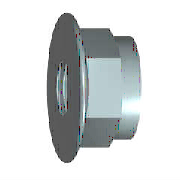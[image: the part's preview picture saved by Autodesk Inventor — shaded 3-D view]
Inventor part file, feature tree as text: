
AUTODESK INVENTOR PART (.ipt)
format: ipt  version: 2018 (Build 220112000, 112)  size: 214,016 bytes
history: native  units: mm (DEFAULTED — no unit token found)
features: other x3, sketch x3, extrude x2, hole x1, plane x1
ambient origin geometry x7: Origin, YZ Plane, XZ Plane, X Axis, Y Axis, Z Axis, Center Point
bodies: Solid1 (feature_tree)
feature tree (10):
  other  "Anello"
  extrude  "Corpo"  Depth=34.5mm
  extrude  "Corona"  Depth=2.4mm
  hole  "Filettatura"  [1 undecoded]
  other  "Smusso1"
  other  "Work Axis1"
  plane  "Work Plane1"
  sketch  "Schizzo1"
  sketch  "Schizzo5"
  sketch  "Schizzo3"
note: 1 required parameter value undecoded (feature->parameter linkage not recoverable at this tier; creation-order binding heuristic only, values carry confidence <= 0.55)
